# Revit family: Bath-Valves_and_Controls-KOHLER-K-300
name_source: partatom
category: Plumbing Fixtures
revit_build: Autodesk Revit 2015 (Build: 20140606_1530(x64)
units: mm (PartAtom-declared; Revit-internal decimal feet)

## types (2) — shared parameters
ADA Compliant = No
Assembly Code = D2020
CW Connection = Yes
Cold Water Inlet = Cold Water Inlet
Date Modified = 01/22/2019
Default Elevation = 36"
Finish = Kohler-Metal-Brass
HW Connection = Yes
Height = 2"
Hot Water Inlet = Hot Water Inlet
Length = 7 7/16"
Manufacturer = KOHLER Co.
MasterFormat 1995 = 154300
MasterFormat 2004 = 22.11.00
Material = Brass construction
Pressure = 0.00 psi
Product Documentation Link = https://www.us.kohler.com
Product Name = High Flow
Product Page URL = http://www.us.kohler.com
URL = https://www.us.kohler.com
Vent Connection = No
Waste Connection = No
Waste Water Outlet = Waste Water Outlet
Width = 8"

## per-type parameters (varying)
| type | Description | Flow Rate | Model | Rigid Connections | Type |
| OD Supplied By Installer | ½ Inch ceramic high-flow valve system | 17 GPM | K-300-K-NA | No | 1 |
| OD With Rigid Connections | ½ Inch ceramic high-flow valve with rigid connections | 0 GPM | K-300-KR-NA | Yes | 2 |

## geometry (parser evidence)
native form markers: Sweep x5
no freeform markers — native parametric forms only
